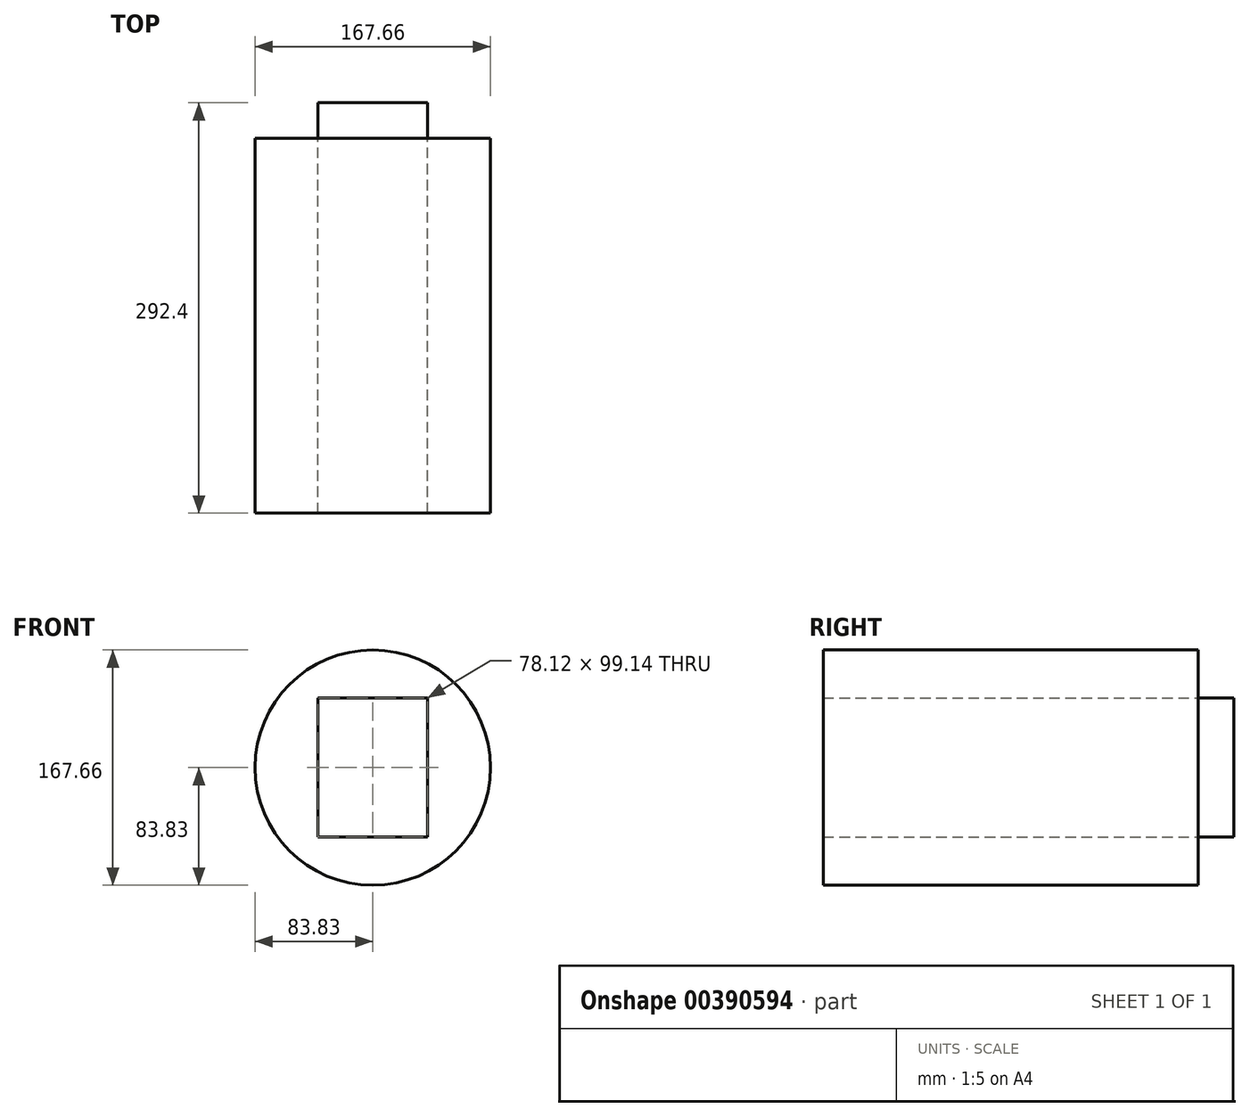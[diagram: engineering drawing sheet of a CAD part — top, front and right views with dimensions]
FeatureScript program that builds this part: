
annotation { "Feature Type Name" : "Feature", "Feature Type Description" : "" }
export const myFeature = defineFeature(function(context is Context, id is Id, definition is map)
    precondition{}
    {
        {
            var Q0;
            Q0=qCreatedBy(makeId("Front.planeOp"),FACE);
            var sketch = newSketch(context, id + "F0", { "sketchPlane" : qUnion([Q0])});
            skLineSegment(sketch, "E0.bottom", {"start": v(0, 0) * mm, "end": v(0, 0) * mm});
            skLineSegment(sketch, "E0.top", {"start": v(0, 0) * mm, "end": v(0, 0) * mm});
            skLineSegment(sketch, "E0.left", {"start": v(0, 0) * mm, "end": v(0, 0) * mm});
            skLineSegment(sketch, "E0.right", {"start": v(0, 0) * mm, "end": v(0, 0) * mm});
            skPoint(sketch, "E0.middle", {"position": v(0, 0) * mm});
            skLineSegment(sketch, "E1.bottom", {"start": v(39.06, 49.57) * mm, "end": v(-39.06, 49.57) * mm});
            skLineSegment(sketch, "E1.top", {"start": v(39.06, -49.57) * mm, "end": v(-39.06, -49.57) * mm});
            skLineSegment(sketch, "E1.left", {"start": v(39.06, 49.57) * mm, "end": v(39.06, -49.57) * mm});
            skLineSegment(sketch, "E1.right", {"start": v(-39.06, 49.57) * mm, "end": v(-39.06, -49.57) * mm});
            skSolve(sketch);
        }
        {
            var Q0;
            Q0=makeQuery(id+"F0.imprint","IMPRINT",FACE,{"disambiguationData":[TD([[makeQuery(id+"F0.imprint","IMPRINT",EDGE,{"derivedFrom":sQuery(id+"F0.wireOp",EDGE,"E1.bottom")}),1.0]])]});
            extrude(context, id + "F1", {"entities" : qUnion([Q0]), "depth" : 25.4 * mm});
        }
        {
            var Q0;
            Q0=makeQuery(id+"F1.opExtrude","CAP_FACE",FACE,{"disambiguationData":[OSD([sQuery(id+"F0.wireOp",EDGE,"E1.bottom"),sQuery(id+"F0.wireOp",EDGE,"E1.top"),sQuery(id+"F0.wireOp",EDGE,"E1.left"),sQuery(id+"F0.wireOp",EDGE,"E1.right")])],"isStart":false});
            var sketch = newSketch(context, id + "F2", { "sketchPlane" : qUnion([Q0])});
            skCircle(sketch, "E2", {"center": v(0, 0) * mm, "radius": 83.83 * mm});
            skSolve(sketch);
        }
        {
            var Q0;
            Q0=makeQuery(id+"F2.imprint","IMPRINT",FACE,{"disambiguationData":[TD([[makeQuery(id+"F2.imprint","IMPRINT",EDGE,{"derivedFrom":sQuery(id+"F2.wireOp",EDGE,"E2")}),1.0]])]});
            extrude(context, id + "F3", {"entities" : qUnion([Q0]), "depth" : 267 * mm});
        }
    });
